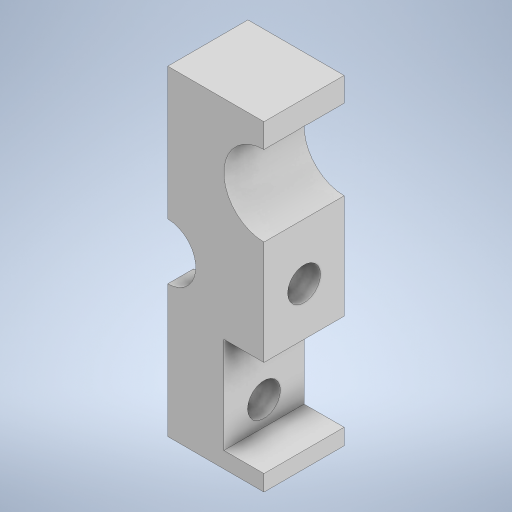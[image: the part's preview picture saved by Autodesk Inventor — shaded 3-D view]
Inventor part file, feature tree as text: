
AUTODESK INVENTOR PART (.ipt)
format: ipt  version: 2023 (Build 270158000, 158)  size: 320,512 bytes
history: native  units: mm
features: extrude x7, sketch x7, plane x1
ambient origin geometry x8: Origin, YZ Plane, XZ Plane, XY Plane, X Axis, Y Axis, Z Axis, Center Point
bodies: Solid1 (feature_tree)
feature tree (15):
  extrude  "Extrusion1"  Depth=20.0mm
  plane  "Work Plane1"
  extrude  "Extrusion2"  Depth=2.0mm
  extrude  "Extrusion3"  Depth=4.0mm
  extrude  "Extrusion4"  Depth=5.0mm TaperAngle=0.0deg
  extrude  "Extrusion5"  Depth=1.8mm TaperAngle=0.0deg
  extrude  "Extrusion6"  Depth=8.0mm TaperAngle=0.0deg
  extrude  "Extrusion7"  Depth=10.0mm
  sketch  "Sketch1"  dims[d0=20.0mm d1=20.0mm]
  sketch  "Sketch2"  dims[d2=4.0mm d6=2.0mm]
  sketch  "Sketch3"  dims[d7=2.0mm d8=4.0mm]
  sketch  "Sketch4"  dims[d9=2.0mm d10=5.0mm d11=0.0mm]
  sketch  "Sketch5"  dims[d12=5.5mm d13=1.8mm d14=0.0mm]
  sketch  "Sketch6"  dims[d15=3.5mm d16=8.0mm d17=0.0mm]
  sketch  "Sketch7"  dims[d18=2.05mm d19=2.05mm d20=2.5mm d21=2.5mm d22=2.5mm d23=2.5mm d24=25.0mm d25=0.0mm d30=5.0mm d31=0.0mm d32=2.5mm d33=1.0mm d34=6.0mm d35=5.0mm d36=4.0mm d37=5.0mm d38=0.0mm d39=2.5mm d40=10.0mm d41=2.05mm d42=20.0mm d43=0.0mm]
